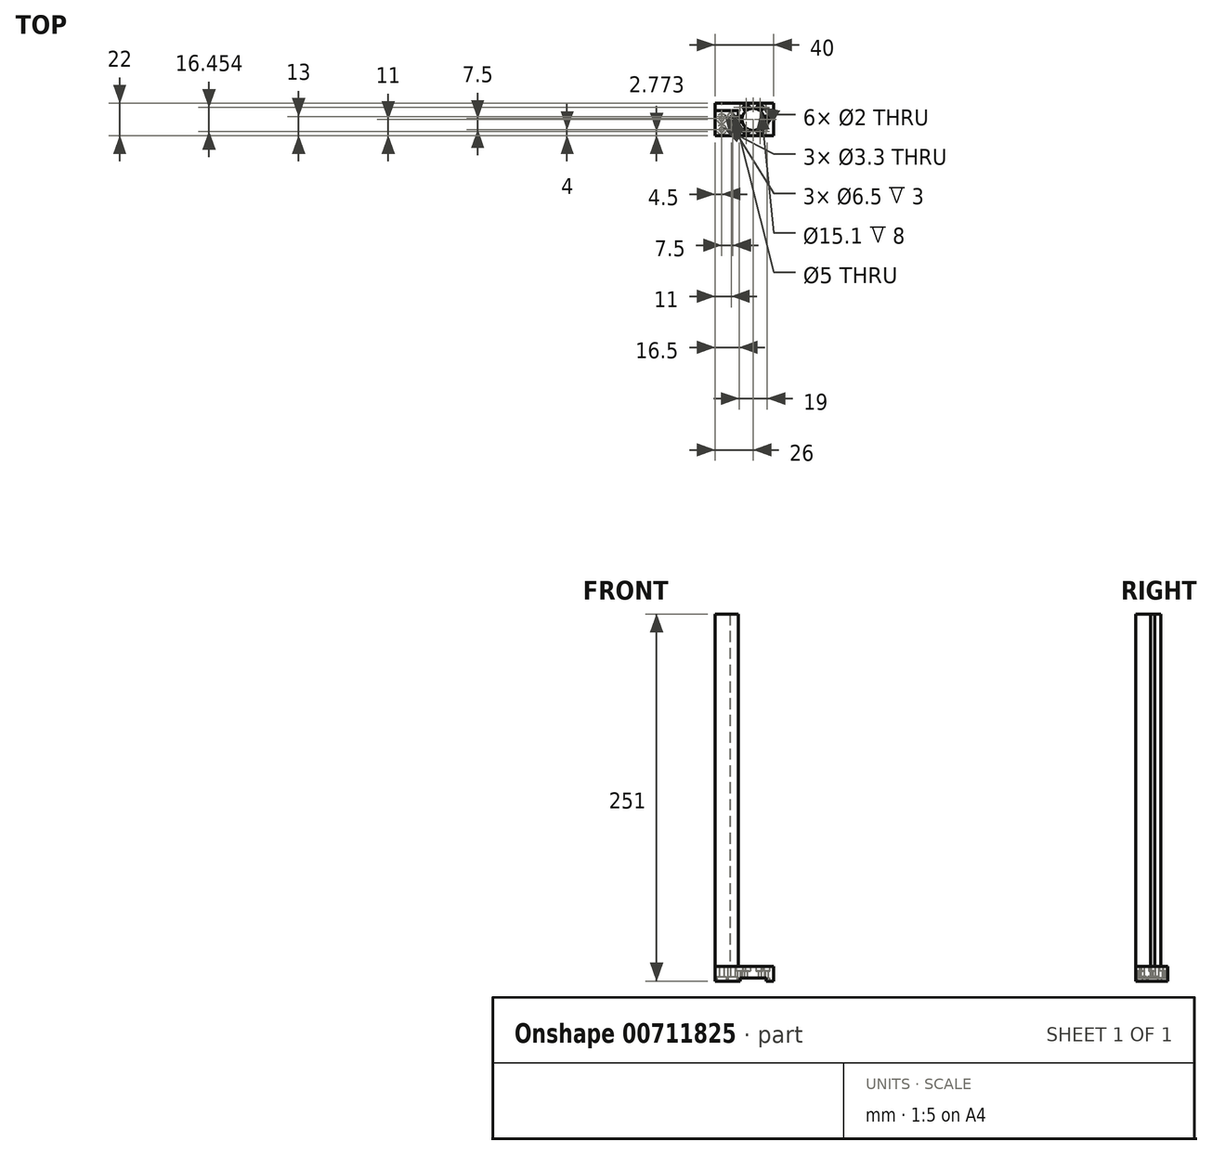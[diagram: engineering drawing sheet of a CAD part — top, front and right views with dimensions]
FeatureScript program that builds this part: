
annotation { "Feature Type Name" : "Feature", "Feature Type Description" : "" }
export const myFeature = defineFeature(function(context is Context, id is Id, definition is map)
    precondition{}
    {
        {
            var Q0;
            Q0=qCreatedBy(makeId("Top.planeOp"),FACE);
            var sketch = newSketch(context, id + "F0", { "sketchPlane" : qUnion([Q0])});
            skLineSegment(sketch, "E0.bottom", {"start": v(0, 0) * mm, "end": v(40, 0) * mm});
            skLineSegment(sketch, "E0.top", {"start": v(0, 22) * mm, "end": v(40, 22) * mm});
            skLineSegment(sketch, "E0.left", {"start": v(0, 0) * mm, "end": v(0, 22) * mm});
            skLineSegment(sketch, "E0.right", {"start": v(40, 0) * mm, "end": v(40, 22) * mm});
            skCircle(sketch, "E1", {"center": v(26, 11) * mm, "radius": 7.55 * mm});
            skCircle(sketch, "E2", {"center": v(11, 13) * mm, "radius": 2.5 * mm});
            skSolve(sketch);
        }
        {
            var Q0;
            Q0=makeQuery(id+"F0.imprint","IMPRINT",FACE,{"disambiguationData":[TD([[makeQuery(id+"F0.imprint","IMPRINT",EDGE,{"derivedFrom":sQuery(id+"F0.wireOp",EDGE,"E0.bottom")}),1.0]])]});
            extrude(context, id + "F1", {"entities" : qUnion([Q0]), "depth" : 10 * mm, "offsetDistance" : 25 * mm});
        }
        {
            var Q0;
            Q0=makeQuery(id+"F1.opExtrude","CAP_FACE",FACE,{"disambiguationData":[OSD([sQuery(id+"F0.wireOp",EDGE,"E0.bottom"),sQuery(id+"F0.wireOp",EDGE,"E0.top"),sQuery(id+"F0.wireOp",EDGE,"E0.left"),sQuery(id+"F0.wireOp",EDGE,"E0.right"),sQuery(id+"F0.wireOp",EDGE,"E1")])],"isStart":false});
            var sketch = newSketch(context, id + "F2", { "sketchPlane" : qUnion([Q0])});
            skCircle(sketch, "E3.cCircle", {"center": v(26, 11) * mm, "radius": 9.5 * mm, "construction": true});
            skLineSegment(sketch, "E3.0", {"start": v(21.25, 19.23) * mm, "end": v(30.75, 19.23) * mm});
            skLineSegment(sketch, "E3.1", {"start": v(30.75, 19.23) * mm, "end": v(35.5, 11) * mm});
            skLineSegment(sketch, "E3.2", {"start": v(35.5, 11) * mm, "end": v(30.75, 2.77) * mm});
            skLineSegment(sketch, "E3.3", {"start": v(30.75, 2.77) * mm, "end": v(21.25, 2.77) * mm});
            skLineSegment(sketch, "E3.4", {"start": v(21.25, 2.77) * mm, "end": v(16.5, 11) * mm});
            skLineSegment(sketch, "E3.5", {"start": v(16.5, 11) * mm, "end": v(21.25, 19.23) * mm});
            skLineSegment(sketch, "E4", {"start": v(30.75, 19.23) * mm, "end": v(21.25, 2.77) * mm, "construction": true});
            skPoint(sketch, "E5", {"position": v(21.25, 19.23) * mm});
            skPoint(sketch, "E6", {"position": v(16.5, 11) * mm});
            skPoint(sketch, "E7", {"position": v(21.25, 2.77) * mm});
            skPoint(sketch, "E8", {"position": v(30.75, 2.77) * mm});
            skPoint(sketch, "E9", {"position": v(35.5, 11) * mm});
            skPoint(sketch, "E10", {"position": v(30.75, 19.23) * mm});
            skSolve(sketch);
        }
        {
            var Q0;
            Q0=sQuery(id+"F2.wireOp",VERTEX,"E5");
            var Q1;
            Q1=sQuery(id+"F2.wireOp",VERTEX,"E6");
            var Q2;
            Q2=sQuery(id+"F2.wireOp",VERTEX,"E7");
            var Q3;
            Q3=sQuery(id+"F2.wireOp",VERTEX,"E8");
            var Q4;
            Q4=sQuery(id+"F2.wireOp",VERTEX,"E9");
            var Q5;
            Q5=sQuery(id+"F2.wireOp",VERTEX,"E10");
            var Q6;
            Q6=makeQuery(id+"F1.opExtrude","SWEPT_BODY",BODY,{"disambiguationData":[OSD([sQuery(id+"F0.wireOp",EDGE,"E0.bottom"),sQuery(id+"F0.wireOp",EDGE,"E0.top"),sQuery(id+"F0.wireOp",EDGE,"E0.left"),sQuery(id+"F0.wireOp",EDGE,"E0.right"),sQuery(id+"F0.wireOp",EDGE,"E1")])]});
            hole(context, id + "F3", {"style" : HoleStyle.SIMPLE, "endStyle" : HoleEndStyle.THROUGH, "holeDiameter" : 2 * mm, "majorDiameter" : 5 * mm, "isTappedThrough" : true, "tappedDepth" : 7 * mm, "tapClearance" : 2, "startFromSketch" : true, "locations" : qUnion([Q0, Q1, Q2, Q3, Q4, Q5]), "scope" : qUnion([Q6])});
        }
        {
            var Q0;
            Q0=makeQuery(id+"F1.opExtrude","CAP_FACE",FACE,{"disambiguationData":[OSD([sQuery(id+"F0.wireOp",EDGE,"E0.bottom"),sQuery(id+"F0.wireOp",EDGE,"E0.top"),sQuery(id+"F0.wireOp",EDGE,"E0.left"),sQuery(id+"F0.wireOp",EDGE,"E0.right"),sQuery(id+"F0.wireOp",EDGE,"E1")])],"isStart":true});
            var sketch = newSketch(context, id + "F4", { "sketchPlane" : qUnion([Q0])});
            skCircle(sketch, "E11", {"center": v(26, -11) * mm, "radius": 11.1 * mm});
            skLineSegment(sketch, "E12.bottom", {"start": v(17, 1.93) * mm, "end": v(35, 1.93) * mm});
            skLineSegment(sketch, "E12.top", {"start": v(17, -23.84) * mm, "end": v(35, -23.84) * mm});
            skLineSegment(sketch, "E12.left", {"start": v(17, 1.93) * mm, "end": v(17, -23.84) * mm});
            skLineSegment(sketch, "E12.right", {"start": v(35, 1.93) * mm, "end": v(35, -23.84) * mm});
            skLineSegment(sketch, "E13", {"start": v(26, 1.93) * mm, "end": v(26, -23.84) * mm, "construction": true});
            skSolve(sketch);
        }
        {
            var Q0;
            Q0 = qSketchRegion(id + "F4", true);
            extrude(context, id + "F5", {"entities" : qUnion([Q0]), "operationType" : NewBodyOperationType.REMOVE, "oppositeDirection" : true, "depth" : 2 * mm, "offsetDistance" : 25 * mm});
        }
        {
            var Q0;
            Q0=makeQuery(id+"F1.opExtrude","CAP_FACE",FACE,{"disambiguationData":[OSD([sQuery(id+"F0.wireOp",EDGE,"E0.bottom"),sQuery(id+"F0.wireOp",EDGE,"E0.top"),sQuery(id+"F0.wireOp",EDGE,"E0.left"),sQuery(id+"F0.wireOp",EDGE,"E0.right"),sQuery(id+"F0.wireOp",EDGE,"E1")])],"isStart":false});
            var sketch = newSketch(context, id + "F6", { "sketchPlane" : qUnion([Q0])});
            skCircle(sketch, "E14", {"center": v(21.25, 19.23) * mm, "radius": 2.05 * mm});
            skCircle(sketch, "E15", {"center": v(30.75, 2.77) * mm, "radius": 2.05 * mm});
            skLineSegment(sketch, "E16", {"start": v(19.47, 18.2) * mm, "end": v(28.97, 1.75) * mm});
            skLineSegment(sketch, "E17", {"start": v(23.03, 20.25) * mm, "end": v(32.53, 3.8) * mm});
            skCircle(sketch, "E18.1.0", {"center": v(21.25, 2.77) * mm, "radius": 2.05 * mm});
            skCircle(sketch, "E18.1.1", {"center": v(30.75, 19.23) * mm, "radius": 2.05 * mm});
            skLineSegment(sketch, "E18.1.2", {"start": v(19.47, 3.8) * mm, "end": v(28.97, 20.25) * mm});
            skLineSegment(sketch, "E18.1.3", {"start": v(23.03, 1.75) * mm, "end": v(32.53, 18.2) * mm});
            skCircle(sketch, "E18.2.0", {"center": v(35.5, 11) * mm, "radius": 2.05 * mm});
            skCircle(sketch, "E18.2.1", {"center": v(16.5, 11) * mm, "radius": 2.05 * mm});
            skLineSegment(sketch, "E18.2.2", {"start": v(35.5, 8.95) * mm, "end": v(16.5, 8.95) * mm});
            skLineSegment(sketch, "E18.2.3", {"start": v(35.5, 13.05) * mm, "end": v(16.5, 13.05) * mm});
            skPoint(sketch, "E18.center", {"position": v(26, 11) * mm});
            skSolve(sketch);
        }
        {
            var Q0;
            Q0 = qSketchRegion(id + "F6", true);
            extrude(context, id + "F7", {"entities" : qUnion([Q0]), "operationType" : NewBodyOperationType.REMOVE, "oppositeDirection" : true, "depth" : 3 * mm, "offsetDistance" : 25 * mm});
        }
        {
            var Q0;
            Q0=makeQuery(id+"F1.opExtrude","CAP_FACE",FACE,{"disambiguationData":[OSD([sQuery(id+"F0.wireOp",EDGE,"E0.bottom"),sQuery(id+"F0.wireOp",EDGE,"E0.top"),sQuery(id+"F0.wireOp",EDGE,"E0.left"),sQuery(id+"F0.wireOp",EDGE,"E0.right"),sQuery(id+"F0.wireOp",EDGE,"E1"),sQuery(id+"F0.wireOp",EDGE,"E2")])],"isStart":false});
            var sketch = newSketch(context, id + "F8", { "sketchPlane" : qUnion([Q0])});
            skLineSegment(sketch, "E19.bottom", {"start": v(0, 0) * mm, "end": v(16, 0) * mm});
            skLineSegment(sketch, "E19.top", {"start": v(0, 17) * mm, "end": v(16, 17) * mm});
            skLineSegment(sketch, "E19.left", {"start": v(0, 0) * mm, "end": v(0, 17) * mm});
            skLineSegment(sketch, "E19.right", {"start": v(16, 0) * mm, "end": v(16, 10) * mm});
            skLineSegment(sketch, "E20.bottom", {"start": v(16, 13) * mm, "end": v(10, 13) * mm});
            skLineSegment(sketch, "E20.top", {"start": v(16, 10) * mm, "end": v(10, 10) * mm});
            skLineSegment(sketch, "E20.right", {"start": v(10, 13) * mm, "end": v(10, 10) * mm});
            skLineSegment(sketch, "E21.trimOffspring", {"start": v(16, 13) * mm, "end": v(16, 17) * mm});
            skSolve(sketch);
        }
        {
            var Q0;
            Q0 = qSketchRegion(id + "F8", true);
            extrude(context, id + "F9", {"entities" : qUnion([Q0]), "depth" : 241 * mm, "offsetDistance" : 25 * mm});
        }
        {
            var Q0;
            {var subQ0=sQuery(id+"F0.wireOp",EDGE,"E2");var subQ1=sQuery(id+"F0.wireOp",EDGE,"E0.left");var subQ3=sQuery(id+"F0.wireOp",EDGE,"E0.top");var subQ8=sQuery(id+"F0.wireOp",EDGE,"E0.bottom");Q0=makeQuery(id+"F5.boolean.opBoolean","SPLIT",FACE,{"disambiguationData":[TD([makeQuery(id+"F1.opExtrude","SWEPT_FACE",FACE,{"disambiguationData":[OSD([subQ1])]})])],"derivedFrom":makeQuery(id+"F1.opExtrude","CAP_FACE",FACE,{"disambiguationData":[OSD([subQ8,subQ3,subQ1,sQuery(id+"F0.wireOp",EDGE,"E0.right"),sQuery(id+"F0.wireOp",EDGE,"E1"),subQ0])],"isStart":true})});}
            var sketch = newSketch(context, id + "F10", { "sketchPlane" : qUnion([Q0])});
            skLineSegment(sketch, "E22", {"start": v(0, -4) * mm, "end": v(43.41, -4) * mm, "construction": true});
            skPoint(sketch, "E23", {"position": v(4.5, -4) * mm});
            skPoint(sketch, "E24", {"position": v(12, -4) * mm});
            skLineSegment(sketch, "E25", {"start": v(4.5, -4) * mm, "end": v(4.5, -22) * mm, "construction": true});
            skPoint(sketch, "E26", {"position": v(4.5, -11.5) * mm});
            skSolve(sketch);
        }
        {
            var Q0;
            Q0=sQuery(id+"F10.wireOp",VERTEX,"E23");
            var Q1;
            Q1=sQuery(id+"F10.wireOp",VERTEX,"E24");
            var Q2;
            Q2=sQuery(id+"F10.wireOp",VERTEX,"E26");
            var Q3;
            Q3=makeQuery(id+"F1.opExtrude","SWEPT_BODY",BODY,{"disambiguationData":[OSD([sQuery(id+"F0.wireOp",EDGE,"E0.bottom"),sQuery(id+"F0.wireOp",EDGE,"E0.top"),sQuery(id+"F0.wireOp",EDGE,"E0.left"),sQuery(id+"F0.wireOp",EDGE,"E0.right"),sQuery(id+"F0.wireOp",EDGE,"E1"),sQuery(id+"F0.wireOp",EDGE,"E2")])]});
            var Q4;
            Q4=makeQuery(id+"F9.opExtrude","SWEPT_BODY",BODY,{"disambiguationData":[OSD([sQuery(id+"F8.wireOp",EDGE,"DilpQjDy-6T43-81H0-YJtb-u8xS9kykDous.bottom"),sQuery(id+"F8.wireOp",EDGE,"DilpQjDy-6T43-81H0-YJtb-u8xS9kykDous.top"),sQuery(id+"F8.wireOp",EDGE,"DilpQjDy-6T43-81H0-YJtb-u8xS9kykDous.left"),sQuery(id+"F8.wireOp",EDGE,"DilpQjDy-6T43-81H0-YJtb-u8xS9kykDous.right"),sQuery(id+"F8.wireOp",EDGE,"wc90iAp1-2MYo-ZfOh-PoDx-YD2zVBdzanqD.bottom"),sQuery(id+"F8.wireOp",EDGE,"wc90iAp1-2MYo-ZfOh-PoDx-YD2zVBdzanqD.top"),sQuery(id+"F8.wireOp",EDGE,"wc90iAp1-2MYo-ZfOh-PoDx-YD2zVBdzanqD.right"),sQuery(id+"F8.wireOp",EDGE,"4emj1twQ-cmTa-fYOj-MFfQ-4Z6FgJfWKCkR.bottom"),sQuery(id+"F8.wireOp",EDGE,"4emj1twQ-cmTa-fYOj-MFfQ-4Z6FgJfWKCkR.top"),sQuery(id+"F8.wireOp",EDGE,"4emj1twQ-cmTa-fYOj-MFfQ-4Z6FgJfWKCkR.right"),sQuery(id+"F8.wireOp",EDGE,"c01cbfef-cb14-48a2-8b9a-ee839d1a60cc.trimOffspring")])]});
            hole(context, id + "F11", {"style" : HoleStyle.C_BORE, "endStyle" : HoleEndStyle.BLIND, "standardTappedOrClearance" : lookupTablePath({ "standard" : "ISO", "fit" : "Normal", "size" : "M3", "type" : "Clearance" }), "standardBlindInLast" : lookupTablePath({ "fit" : "Standard", "standard" : "ISO", "size" : "M3", "type" : "Clearance" }), "holeDiameter" : 3.3 * mm, "cBoreDiameter" : 6.5 * mm, "cBoreDepth" : 3 * mm, "majorDiameter" : 5 * mm, "holeDepth" : 20 * mm, "isTappedThrough" : true, "tappedDepth" : 7 * mm, "tapClearance" : 2, "startFromSketch" : true, "locations" : qUnion([Q0, Q1, Q2]), "scope" : qUnion([Q3, Q4])});
        }
    });
